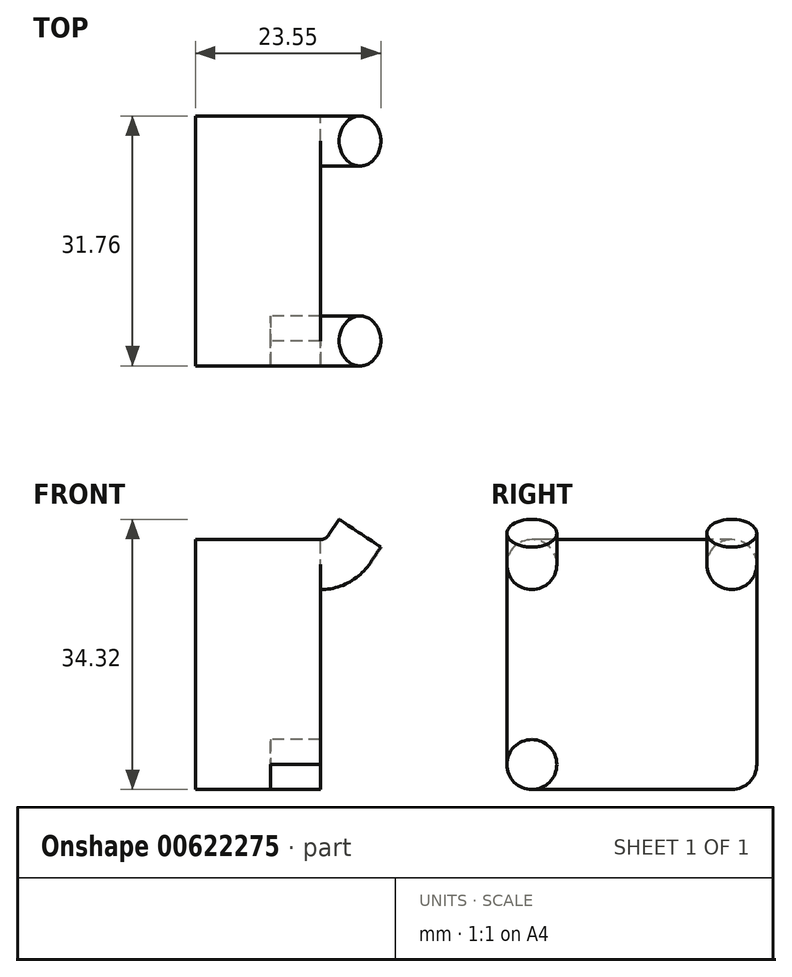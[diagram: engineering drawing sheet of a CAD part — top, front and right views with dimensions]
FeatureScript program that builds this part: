
annotation { "Feature Type Name" : "Feature", "Feature Type Description" : "" }
export const myFeature = defineFeature(function(context is Context, id is Id, definition is map)
    precondition{}
    {
        {
            var Q0;
            Q0=qCreatedBy(makeId("Right.planeOp"),FACE);
            var sketch = newSketch(context, id + "F0", { "sketchPlane" : qUnion([Q0])});
            skLineSegment(sketch, "E0.bottom", {"start": v(15.88, -15.87) * mm, "end": v(-15.88, -15.88) * mm});
            skLineSegment(sketch, "E0.top", {"start": v(15.88, 15.88) * mm, "end": v(-15.88, 15.88) * mm});
            skLineSegment(sketch, "E0.left", {"start": v(15.88, -15.87) * mm, "end": v(15.88, 15.88) * mm});
            skLineSegment(sketch, "E0.right", {"start": v(-15.88, -15.88) * mm, "end": v(-15.88, 15.88) * mm});
            skPoint(sketch, "E0.middle", {"position": v(0, 0) * mm});
            skSolve(sketch);
        }
        {
            var Q0;
            Q0=makeQuery(id+"F0.imprint","IMPRINT",FACE,{"disambiguationData":[TD([[makeQuery(id+"F0.imprint","IMPRINT",EDGE,{"derivedFrom":sQuery(id+"F0.wireOp",EDGE,"E0.bottom")}),-1.0]])]});
            extrude(context, id + "F1", {"entities" : qUnion([Q0]), "depth" : 9.52 * mm, "offsetDistance" : 25.4 * mm});
        }
        {
            var Q0;
            Q0=makeQuery(id+"F1.opExtrude","CAP_FACE",FACE,{"disambiguationData":[OSD([sQuery(id+"F0.wireOp",EDGE,"E0.bottom"),sQuery(id+"F0.wireOp",EDGE,"E0.top"),sQuery(id+"F0.wireOp",EDGE,"E0.left"),sQuery(id+"F0.wireOp",EDGE,"E0.right")])],"isStart":false});
            var sketch = newSketch(context, id + "F2", { "sketchPlane" : qUnion([Q0])});
            skCircle(sketch, "E1", {"center": v(-12.7, 12.7) * mm, "radius": 3.18 * mm});
            skLineSegment(sketch, "E2", {"start": v(-24.57, 0) * mm, "end": v(19.39, 0) * mm, "construction": true});
            skPoint(sketch, "E2.endSnap0", {"position": v(-15.88, 0) * mm});
            skLineSegment(sketch, "E3", {"start": v(0, 20.38) * mm, "end": v(0, -18.88) * mm, "construction": true});
            skCircle(sketch, "E4.MirrorC", {"center": v(-12.7, -12.7) * mm, "radius": 3.18 * mm});
            skLineSegment(sketch, "E5.MirrorCS", {"start": v(0, -20.38) * mm, "end": v(0, 18.88) * mm, "construction": true});
            skCircle(sketch, "E6.MirrorC", {"center": v(12.7, 12.7) * mm, "radius": 3.18 * mm});
            skCircle(sketch, "E7.MirrorC", {"center": v(12.7, -12.7) * mm, "radius": 3.18 * mm});
            skLineSegment(sketch, "E8", {"start": v(-12.7, 15.88) * mm, "end": v(-12.7, -15.88) * mm, "construction": true});
            skLineSegment(sketch, "E9", {"start": v(-15.88, 12.7) * mm, "end": v(15.88, 12.7) * mm, "construction": true});
            skPoint(sketch, "E10", {"position": v(-12.7, 15.88) * mm});
            skPoint(sketch, "E11", {"position": v(0, 0) * mm});
            skSolve(sketch);
        }
        {
            var Q0;
            Q0=makeQuery(id+"F1.opExtrude","SWEPT_FACE",FACE,{"disambiguationData":[OSD([sQuery(id+"F0.wireOp",EDGE,"E0.top")])]});
            var sketch = newSketch(context, id + "F3", { "sketchPlane" : qUnion([Q0])});
            skLineSegment(sketch, "E12", {"start": v(0, -12.7) * mm, "end": v(9.53, -12.7) * mm, "construction": true});
            skSolve(sketch);
        }
        {
            var Q0;
            Q0=sQuery(id+"F3.wireOp",VERTEX,"E12.start");
            var Q1;
            Q1=sQuery(id+"F2.wireOp",VERTEX,"E10");
            var Q2;
            Q2=sQuery(id+"F2.wireOp",VERTEX,"E8.end");
            cPlane(context, id + "F4", {"entities" : qUnion([Q0, Q1, Q2]), "cplaneType" : CPlaneType.THREE_POINT, "offset" : 25.4 * mm, "width" : 152.4 * mm, "height" : 152.4 * mm});
        }
        {
            var Q0;
            Q0=qCreatedBy(id+"F4.planeOp",FACE);
            var sketch = newSketch(context, id + "F5", { "sketchPlane" : qUnion([Q0])});
            skLineSegment(sketch, "E13", {"start": v(9.53, 9.53) * mm, "end": v(9.53, 15.88) * mm});
            skLineSegment(sketch, "E14", {"start": v(9.53, 9.53) * mm, "end": v(15.88, 9.53) * mm});
            skArc(sketch, "E15", {"start": v(15.88, 9.53) * mm, "mid": v(19.48, 10.43) * mm, "end": v(22.23, 12.93) * mm});
            skLineSegment(sketch, "E16", {"start": v(22.23, 12.93) * mm, "end": v(23.55, 14.93) * mm});
            skSolve(sketch);
        }
        {
            var Q0;
            {var subQ0=sQuery(id+"F2.wireOp",EDGE,"E1");var subQ1=makeQuery(id+"F2.imprint","INTERSECT",VERTEX,{"derivedFrom":[makeQuery(id+"F1.opExtrude","CAP_EDGE",EDGE,{"disambiguationData":[OSD([sQuery(id+"F0.wireOp",EDGE,"E0.top")])],"isStart":false}),subQ0]});Q0=makeQuery(id+"F2.imprint","IMPRINT",FACE,{"disambiguationData":[TD([[makeQuery(id+"F2.imprint","IMPRINT",EDGE,{"disambiguationData":[TD([[subQ1,-1.0]])],"derivedFrom":subQ0}),1.0]])]});}
            var Q1;
            Q1 = qSketchRegion(id + "F5", true);
            var Q2;
            Q2=sQuery(id+"F5.wireOp",EDGE,"E14");
            var Q3;
            Q3=sQuery(id+"F5.wireOp",EDGE,"E15");
            var Q4;
            Q4=sQuery(id+"F5.wireOp",EDGE,"E16");
            sweep(context, id + "F6", {"operationType" : NewBodyOperationType.ADD, "profiles" : qUnion([Q0, Q1]), "path" : qUnion([Q2, Q3, Q4])});
        }
        {
            var Q0;
            {var subQ0=sQuery(id+"F0.wireOp",EDGE,"E0.top");Q0=makeQuery(id+"F3.imprint","IMPRINT",FACE,{"disambiguationData":[TD([[makeQuery(id+"F3.imprint","IMPRINT",EDGE,{"derivedFrom":makeQuery(id+"F1.opExtrude","CAP_EDGE",EDGE,{"disambiguationData":[OSD([subQ0])],"isStart":true})}),1.0]])]});}
            var sketch = newSketch(context, id + "F7", { "sketchPlane" : qUnion([Q0])});
            skLineSegment(sketch, "E17", {"start": v(12.55, 0) * mm, "end": v(0, 0) * mm, "construction": true});
            skSolve(sketch);
        }
        {
            var Q0;
            Q0=sQuery(id+"F7.wireOp",VERTEX,"E17.end");
            var Q1;
            Q1=sQuery(id+"F7.wireOp",VERTEX,"E17.start");
            var Q2;
            Q2=sQuery(id+"F2.wireOp",VERTEX,"E11");
            cPlane(context, id + "F8", {"entities" : qUnion([Q0, Q1, Q2]), "cplaneType" : CPlaneType.THREE_POINT, "offset" : 25.4 * mm, "width" : 152.4 * mm, "height" : 152.4 * mm});
        }
        {
            var Q0;
            Q0=makeQuery(id+"F1.opExtrude","SWEPT_BODY",BODY,{"disambiguationData":[OSD([sQuery(id+"F0.wireOp",EDGE,"E0.bottom"),sQuery(id+"F0.wireOp",EDGE,"E0.top"),sQuery(id+"F0.wireOp",EDGE,"E0.left"),sQuery(id+"F0.wireOp",EDGE,"E0.right")])]});
            var Q1;
            Q1=qCreatedBy(id+"F8.planeOp",FACE);
            mirror(context, id + "F9", {"operationType" : NewBodyOperationType.ADD, "entities" : qUnion([Q0]), "mirrorPlane" : qUnion([Q1])});
        }
        {
            var Q0;
            {var subQ0=sQuery(id+"F2.wireOp",EDGE,"E4.MirrorC");var subQ1=makeQuery(id+"F2.imprint","INTERSECT",VERTEX,{"derivedFrom":[makeQuery(id+"F1.opExtrude","CAP_EDGE",EDGE,{"disambiguationData":[OSD([sQuery(id+"F0.wireOp",EDGE,"E0.bottom")])],"isStart":false}),subQ0]});Q0=makeQuery(id+"F2.imprint","IMPRINT",FACE,{"disambiguationData":[TD([[makeQuery(id+"F2.imprint","IMPRINT",EDGE,{"disambiguationData":[TD([[subQ1,-1.0]])],"derivedFrom":subQ0}),-1.0]])]});}
            var Q1;
            {var subQ0=sQuery(id+"F2.wireOp",EDGE,"E7.MirrorC");var subQ1=makeQuery(id+"F2.imprint","INTERSECT",VERTEX,{"derivedFrom":[makeQuery(id+"F1.opExtrude","CAP_EDGE",EDGE,{"disambiguationData":[OSD([sQuery(id+"F0.wireOp",EDGE,"E0.bottom")])],"isStart":false}),subQ0]});Q1=makeQuery(id+"F2.imprint","IMPRINT",FACE,{"disambiguationData":[TD([[makeQuery(id+"F2.imprint","IMPRINT",EDGE,{"disambiguationData":[TD([[subQ1,-1.0]])],"derivedFrom":subQ0}),1.0]])]});}
            extrude(context, id + "F10", {"entities" : qUnion([Q0, Q1]), "operationType" : NewBodyOperationType.ADD, "depth" : 6.35 * mm, "offsetDistance" : 25.4 * mm});
        }
        {
            var Q0;
            Q0=makeQuery(id+"F1.opExtrude","SWEPT_EDGE",EDGE,{"disambiguationData":[OSD([sQuery(id+"F0.wireOp",EDGE,"E0.top"),sQuery(id+"F0.wireOp",EDGE,"E0.right")])]});
            var Q1;
            Q1=makeQuery(id+"F1.opExtrude","SWEPT_EDGE",EDGE,{"disambiguationData":[OSD([sQuery(id+"F0.wireOp",EDGE,"E0.bottom"),sQuery(id+"F0.wireOp",EDGE,"E0.right")])]});
            var Q2;
            Q2=makeQuery(id+"F1.opExtrude","SWEPT_EDGE",EDGE,{"disambiguationData":[OSD([sQuery(id+"F0.wireOp",EDGE,"E0.bottom"),sQuery(id+"F0.wireOp",EDGE,"E0.left")])]});
            var Q3;
            Q3=makeQuery(id+"F1.opExtrude","SWEPT_EDGE",EDGE,{"disambiguationData":[OSD([sQuery(id+"F0.wireOp",EDGE,"E0.top"),sQuery(id+"F0.wireOp",EDGE,"E0.left")])]});
            fillet(context, id + "F11", {"entities" : qUnion([Q0, Q1, Q2, Q3]), "radius" : 3.17 * mm, "tangentPropagation" : true, "allowEdgeOverflow" : false});
        }
    });
